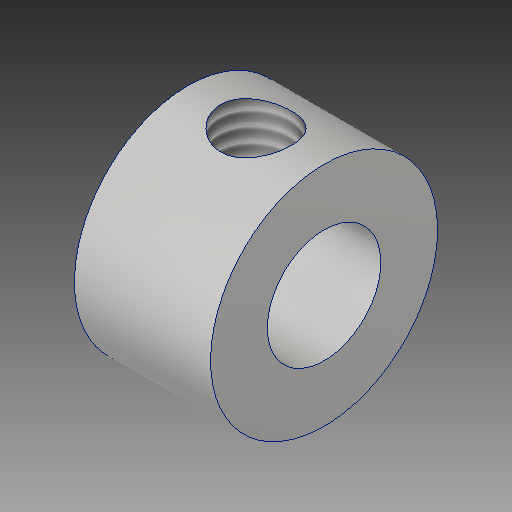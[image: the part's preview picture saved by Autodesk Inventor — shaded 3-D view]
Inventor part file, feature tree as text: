
AUTODESK INVENTOR PART (.ipt)
format: ipt  version: 2019 (Build 230136000, 136)  size: 136,192 bytes
history: native  units: in
note: dims shown in document units (in); Inventor stores cm internally (conversion verified against a paired STEP export)
features: sketch x2, revolve x1, plane x1, hole x1
ambient origin geometry x8: Origin, YZ Plane, XZ Plane, XY Plane, X Axis, Y Axis, Z Axis, Center Point
bodies: Body1 (feature_tree)
feature tree (5):
  revolve  "Revolution1"  [1 undecoded]
  plane  "Work Plane1"
  hole  "Hole1"  [1 undecoded]
  sketch  "Sketch2"  dims[d8=0.3in d9=0.125in]
  sketch  "Sketch3"  dims[d10=0.3in d11=0.125in d12=90.0deg d13=0.156in d14=0.125in d15=0.375in d16=0.25in d17=0.5635in d18=0.125in d19=0.8108in]
note: 2 required parameter values undecoded (feature->parameter linkage not recoverable at this tier; creation-order binding heuristic only, values carry confidence <= 0.55)